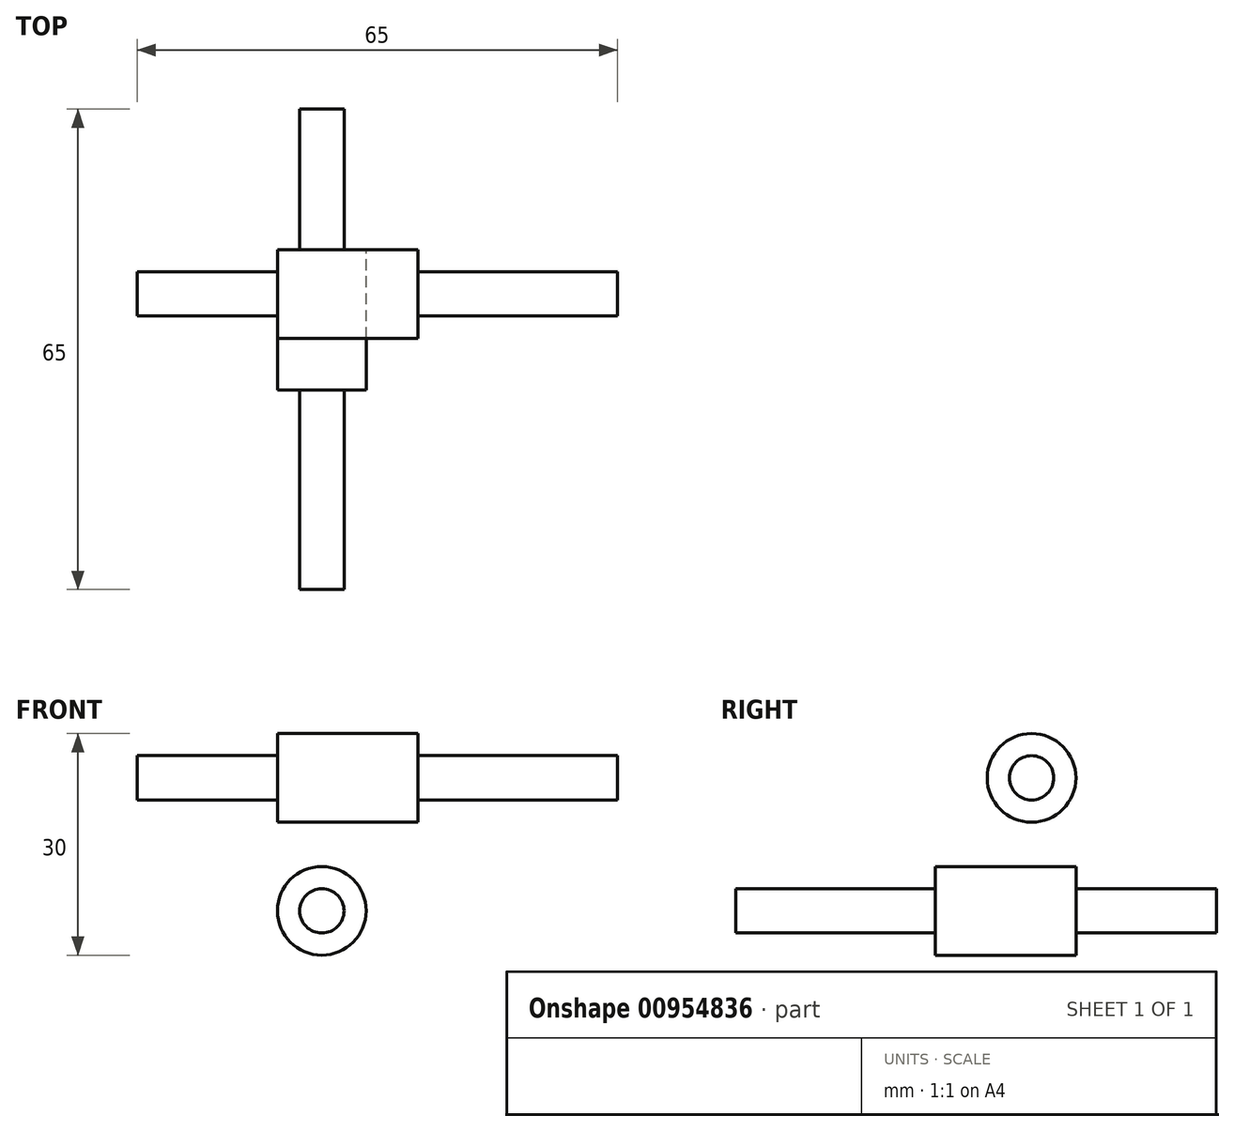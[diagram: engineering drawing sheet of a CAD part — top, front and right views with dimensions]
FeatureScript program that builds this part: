
annotation { "Feature Type Name" : "Feature", "Feature Type Description" : "" }
export const myFeature = defineFeature(function(context is Context, id is Id, definition is map)
    precondition{}
    {
        {
            assignVariable(context, id + "F0", {"variableType" : VariableType.LENGTH, "name" : "BearingOD", "lengthValue" : 12 * mm});
        }
        {
            assignVariable(context, id + "F1", {"variableType" : VariableType.LENGTH, "name" : "BearingL", "lengthValue" : 19 * mm});
        }
        {
            assignVariable(context, id + "F2", {"variableType" : VariableType.LENGTH, "name" : "BearingOverlap", "lengthValue" : getVariable(context, 'BearingOD') / 2});
        }
        {
            var Q0;
            Q0=qCreatedBy(makeId("Front.planeOp"),FACE);
            var sketch = newSketch(context, id + "F3", { "sketchPlane" : qUnion([Q0])});
            skCircle(sketch, "E0", {"center": v(0, -9) * mm, "radius": 3 * mm});
            skCircle(sketch, "E1", {"center": v(0, -9) * mm, "radius": 6 * mm});
            skSolve(sketch);
        }
        {
            var Q0;
            Q0=qCreatedBy(makeId("Right.planeOp"),FACE);
            var sketch = newSketch(context, id + "F4", { "sketchPlane" : qUnion([Q0])});
            skCircle(sketch, "E2", {"center": v(0, 9) * mm, "radius": 3 * mm});
            skCircle(sketch, "E3", {"center": v(0, 9) * mm, "radius": 6 * mm});
            skSolve(sketch);
        }
        {
            var Q0;
            Q0=makeQuery(id+"F4.imprint","IMPRINT",FACE,{"disambiguationData":[TD([[makeQuery(id+"F4.imprint","IMPRINT",EDGE,{"derivedFrom":sQuery(id+"F4.wireOp",EDGE,"E2")}),1.0]])]});
            var Q1;
            Q1=sQuery(id+"F4.wireOp",EDGE,"E2");
            extrude(context, id + "F5", {"entities" : qUnion([Q0]), "surfaceEntities" : qUnion([Q1]), "depth" : 40 * mm, "offsetDistance" : 25 * mm, "hasSecondDirection" : true, "secondDirectionOppositeDirection" : true, "secondDirectionDepth" : 25 * mm});
        }
        {
            var Q0;
            Q0=makeQuery(id+"F4.imprint","IMPRINT",FACE,{"disambiguationData":[TD([[makeQuery(id+"F4.imprint","IMPRINT",EDGE,{"derivedFrom":sQuery(id+"F4.wireOp",EDGE,"E2")}),-1.0]])]});
            extrude(context, id + "F6", {"entities" : qUnion([Q0]), "operationType" : NewBodyOperationType.ADD, "depth" : getVariable(context, 'BearingL') - getVariable(context, 'BearingOverlap'), "offsetDistance" : 25 * mm, "hasSecondDirection" : true, "secondDirectionOppositeDirection" : true, "secondDirectionDepth" : getVariable(context, 'BearingOverlap')});
        }
        {
            var Q0;
            Q0=makeQuery(id+"F3.imprint","IMPRINT",FACE,{"disambiguationData":[TD([[makeQuery(id+"F3.imprint","IMPRINT",EDGE,{"derivedFrom":sQuery(id+"F3.wireOp",EDGE,"E0")}),1.0]])]});
            extrude(context, id + "F7", {"entities" : qUnion([Q0]), "depth" : 40 * mm, "offsetDistance" : 25 * mm, "hasSecondDirection" : true, "secondDirectionOppositeDirection" : true, "secondDirectionDepth" : 25 * mm});
        }
        {
            var Q0;
            Q0=makeQuery(id+"F3.imprint","IMPRINT",FACE,{"disambiguationData":[TD([[makeQuery(id+"F3.imprint","IMPRINT",EDGE,{"derivedFrom":sQuery(id+"F3.wireOp",EDGE,"E0")}),-1.0]])]});
            extrude(context, id + "F8", {"entities" : qUnion([Q0]), "operationType" : NewBodyOperationType.ADD, "depth" : getVariable(context, 'BearingL') - getVariable(context, 'BearingOverlap'), "offsetDistance" : 25 * mm, "hasSecondDirection" : true, "secondDirectionOppositeDirection" : true, "secondDirectionDepth" : getVariable(context, 'BearingOverlap')});
        }
    });
